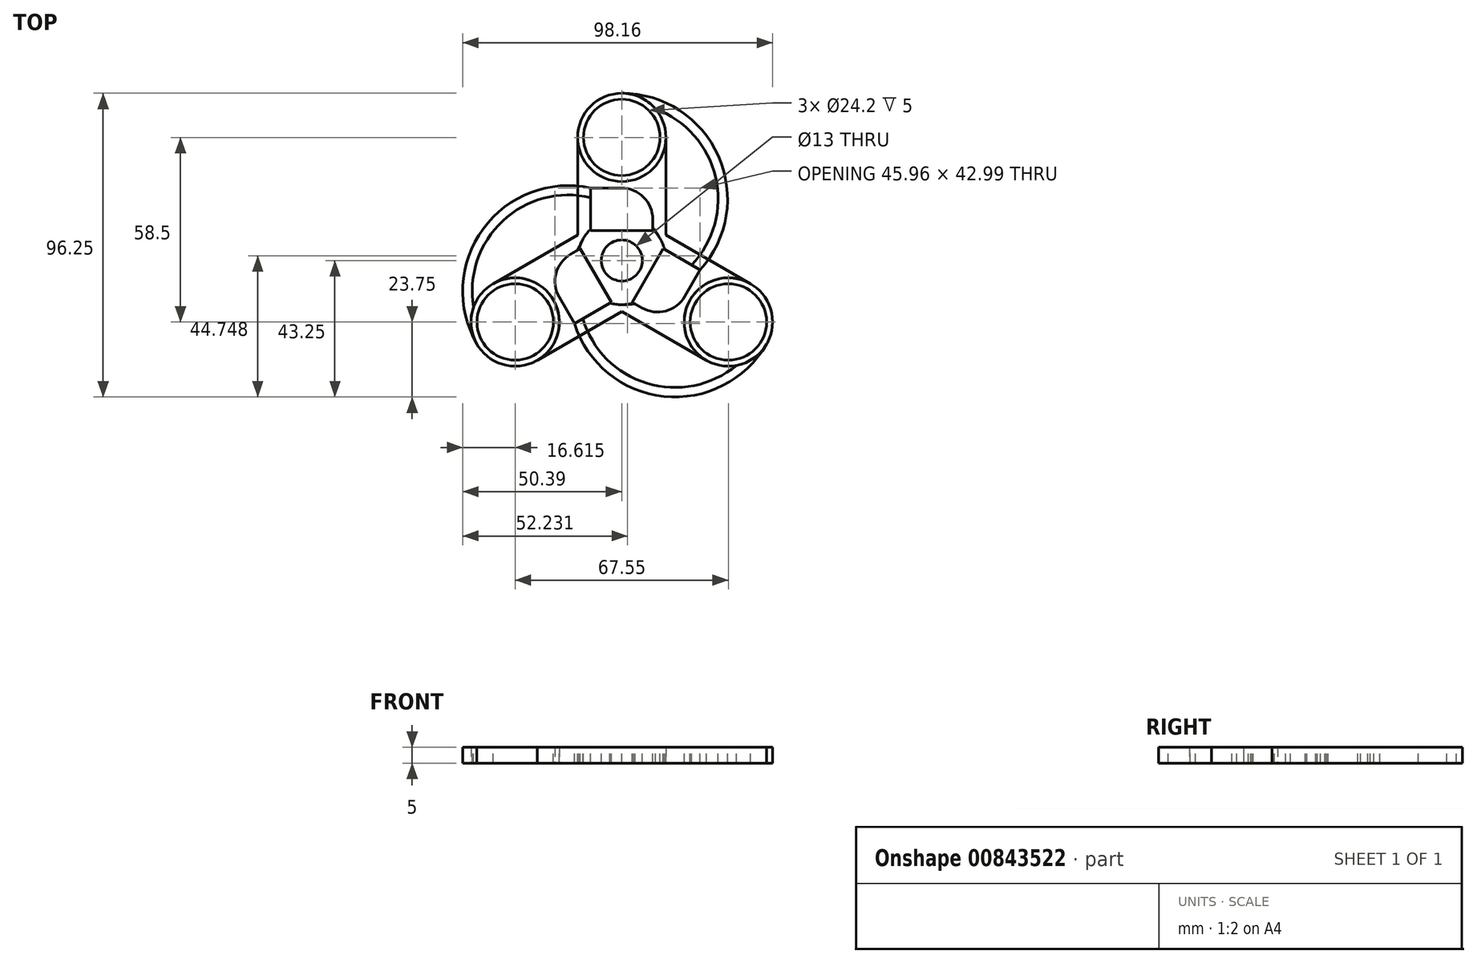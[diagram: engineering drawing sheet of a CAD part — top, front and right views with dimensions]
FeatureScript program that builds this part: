
annotation { "Feature Type Name" : "Feature", "Feature Type Description" : "" }
export const myFeature = defineFeature(function(context is Context, id is Id, definition is map)
    precondition{}
    {
        {
            var Q0;
            Q0=qCreatedBy(makeId("Top.planeOp"),FACE);
            var sketch = newSketch(context, id + "F0", { "sketchPlane" : qUnion([Q0])});
            skCircle(sketch, "E0", {"center": v(0, 0) * mm, "radius": 14 * mm});
            skSolve(sketch);
        }
        {
            var Q0;
            Q0 = qSketchRegion(id + "F0", true);
            extrude(context, id + "F1", {"entities" : qUnion([Q0]), "depth" : 5 * mm, "offsetDistance" : 25 * mm});
        }
        {
            var Q0;
            Q0=makeQuery(id+"F1.opExtrude","CAP_FACE",FACE,{"disambiguationData":[OSD([sQuery(id+"F0.wireOp",EDGE,"E0")])],"isStart":false});
            var sketch = newSketch(context, id + "F2", { "sketchPlane" : qUnion([Q0])});
            skCircle(sketch, "E1", {"center": v(0, 0) * mm, "radius": 6.5 * mm});
            skSolve(sketch);
        }
        {
            var Q0;
            Q0 = qSketchRegion(id + "F2", true);
            var Q1;
            Q1 = qSketchRegion(id + "F4", true);
            extrude(context, id + "F3", {"entities" : qUnion([Q0, Q1]), "operationType" : NewBodyOperationType.REMOVE, "oppositeDirection" : true, "depth" : 5 * mm, "offsetDistance" : 25 * mm});
        }
        {
            var Q0;
            Q0=qCreatedBy(makeId("Top.planeOp"),FACE);
            var sketch = newSketch(context, id + "F4", { "sketchPlane" : qUnion([Q0])});
            skCircle(sketch, "E2", {"center": v(0, 39) * mm, "radius": 14 * mm});
            skCircle(sketch, "E3.1.0", {"center": v(-33.77, -19.5) * mm, "radius": 14 * mm});
            skCircle(sketch, "E3.2.0", {"center": v(33.77, -19.5) * mm, "radius": 14 * mm});
            skPoint(sketch, "E3.center", {"position": v(0, 0) * mm});
            skSolve(sketch);
        }
        {
            var Q0;
            Q0 = qSketchRegion(id + "F4", true);
            extrude(context, id + "F5", {"entities" : qUnion([Q0]), "depth" : 5 * mm, "offsetDistance" : 25 * mm});
        }
        {
            var Q0;
            Q0=makeQuery(id+"F5.opExtrude","CAP_FACE",FACE,{"disambiguationData":[OSD([sQuery(id+"F4.wireOp",EDGE,"E2")])],"isStart":false});
            var sketch = newSketch(context, id + "F6", { "sketchPlane" : qUnion([Q0])});
            skCircle(sketch, "E4", {"center": v(0, 39) * mm, "radius": 12.1 * mm});
            skCircle(sketch, "E5.1.0", {"center": v(-33.77, -19.5) * mm, "radius": 12.1 * mm});
            skCircle(sketch, "E5.2.0", {"center": v(33.77, -19.5) * mm, "radius": 12.1 * mm});
            skPoint(sketch, "E5.center", {"position": v(0, 0) * mm});
            skSolve(sketch);
        }
        {
            var Q0;
            Q0 = qSketchRegion(id + "F6", true);
            extrude(context, id + "F7", {"entities" : qUnion([Q0]), "operationType" : NewBodyOperationType.REMOVE, "oppositeDirection" : true, "depth" : 5 * mm, "offsetDistance" : 25 * mm});
        }
        {
            var Q0;
            Q0=makeQuery(id+"F5.opExtrude","CAP_FACE",FACE,{"disambiguationData":[OSD([sQuery(id+"F4.wireOp",EDGE,"E2")])],"isStart":false});
            var sketch = newSketch(context, id + "F8", { "sketchPlane" : qUnion([Q0])});
            skArc(sketch, "E6", {"start": v(0, -14) * mm, "mid": v(33.5, 19.5) * mm, "end": v(0, 53) * mm});
            skArc(sketch, "E7", {"start": v(10.66, -9.08) * mm, "mid": v(30.5, 19.5) * mm, "end": v(10.66, 48.08) * mm});
            skPoint(sketch, "E7.endSnap0", {"position": v(10.66, 48.08) * mm});
            skArc(sketch, "E8", {"start": v(10.66, 48.08) * mm, "mid": v(5.87, 51.7) * mm, "end": v(0, 53) * mm});
            skArc(sketch, "E9", {"start": v(0, -14) * mm, "mid": v(5.87, -12.7) * mm, "end": v(10.66, -9.08) * mm});
            skArc(sketch, "E10.1.0", {"start": v(12.12, 7) * mm, "mid": v(-33.64, 19.26) * mm, "end": v(-45.9, -26.5) * mm});
            skArc(sketch, "E10.1.1", {"start": v(12.12, 7) * mm, "mid": v(8.07, 11.44) * mm, "end": v(2.53, 13.77) * mm});
            skArc(sketch, "E10.1.2", {"start": v(-46.97, -14.8) * mm, "mid": v(-47.72, -20.77) * mm, "end": v(-45.9, -26.5) * mm});
            skPoint(sketch, "E10.1.3", {"position": v(-46.97, -14.8) * mm});
            skArc(sketch, "E10.1.5", {"start": v(2.53, 13.77) * mm, "mid": v(-32.14, 16.66) * mm, "end": v(-46.97, -14.8) * mm});
            skArc(sketch, "E10.2.0", {"start": v(-12.12, 7) * mm, "mid": v(0.14, -38.76) * mm, "end": v(45.9, -26.5) * mm});
            skArc(sketch, "E10.2.1", {"start": v(-12.12, 7) * mm, "mid": v(-13.94, 1.27) * mm, "end": v(-13.2, -4.7) * mm});
            skArc(sketch, "E10.2.2", {"start": v(36.3, -33.27) * mm, "mid": v(41.85, -30.94) * mm, "end": v(45.9, -26.5) * mm});
            skPoint(sketch, "E10.2.3", {"position": v(36.3, -33.27) * mm});
            skArc(sketch, "E10.2.5", {"start": v(-13.2, -4.7) * mm, "mid": v(1.64, -36.16) * mm, "end": v(36.3, -33.27) * mm});
            skSolve(sketch);
        }
        {
            var Q0;
            Q0 = qSketchRegion(id + "F8", true);
            extrude(context, id + "F9", {"entities" : qUnion([Q0]), "oppositeDirection" : true, "depth" : 5 * mm, "offsetDistance" : 25 * mm});
        }
        {
            var Q0;
            Q0=makeQuery(id+"F9.opExtrude","CAP_FACE",FACE,{"disambiguationData":[OSD([sQuery(id+"F8.wireOp",EDGE,"E6"),sQuery(id+"F8.wireOp",EDGE,"dLtM4N0n-psE5-noLE-qL9G-tePY1SIvNnSB"),sQuery(id+"F8.wireOp",EDGE,"YNhRmu4X-lJfx-RaQj-FMsx-qZMkfT5EsRf2"),sQuery(id+"F8.wireOp",EDGE,"4TdKvFUL-VVMQ-oNHD-A8zk-RRuQfqVaMpFy"),sQuery(id+"F8.wireOp",EDGE,"a4ac8118-5000-4600-9653-84e8d269efdb.1.0"),sQuery(id+"F8.wireOp",EDGE,"a4ac8118-5000-4600-9653-84e8d269efdb.1.1"),sQuery(id+"F8.wireOp",EDGE,"a4ac8118-5000-4600-9653-84e8d269efdb.1.2"),sQuery(id+"F8.wireOp",EDGE,"a4ac8118-5000-4600-9653-84e8d269efdb.1.3"),sQuery(id+"F8.wireOp",EDGE,"a4ac8118-5000-4600-9653-84e8d269efdb.2.0"),sQuery(id+"F8.wireOp",EDGE,"a4ac8118-5000-4600-9653-84e8d269efdb.2.1"),sQuery(id+"F8.wireOp",EDGE,"a4ac8118-5000-4600-9653-84e8d269efdb.2.2"),sQuery(id+"F8.wireOp",EDGE,"a4ac8118-5000-4600-9653-84e8d269efdb.2.3")])],"isStart":true});
            var sketch = newSketch(context, id + "F10", { "sketchPlane" : qUnion([Q0])});
            skLineSegment(sketch, "E11.left", {"start": v(-14, 0) * mm, "end": v(-14, 39) * mm});
            skLineSegment(sketch, "E11.right", {"start": v(14, 0) * mm, "end": v(14, 39) * mm});
            skPoint(sketch, "E12.center", {"position": v(0, 0) * mm});
            skArc(sketch, "E13", {"start": v(-14, 39) * mm, "mid": v(0, 25) * mm, "end": v(14, 39) * mm});
            skArc(sketch, "E14", {"start": v(14, 0) * mm, "mid": v(0, 14) * mm, "end": v(-14, 0) * mm});
            skArc(sketch, "E15.1.0", {"start": v(-7, 12.12) * mm, "mid": v(-12.12, -7) * mm, "end": v(7, -12.12) * mm});
            skLineSegment(sketch, "E15.1.1", {"start": v(-7, 12.12) * mm, "end": v(-40.77, -7.38) * mm});
            skArc(sketch, "E15.1.2", {"start": v(-26.77, -31.62) * mm, "mid": v(-21.65, -12.5) * mm, "end": v(-40.77, -7.38) * mm});
            skLineSegment(sketch, "E15.1.3", {"start": v(7, -12.12) * mm, "end": v(-26.77, -31.62) * mm});
            skArc(sketch, "E15.2.0", {"start": v(-7, -12.12) * mm, "mid": v(12.12, -7) * mm, "end": v(7, 12.12) * mm});
            skLineSegment(sketch, "E15.2.1", {"start": v(-7, -12.12) * mm, "end": v(26.77, -31.62) * mm});
            skArc(sketch, "E15.2.2", {"start": v(40.77, -7.38) * mm, "mid": v(21.65, -12.5) * mm, "end": v(26.77, -31.62) * mm});
            skLineSegment(sketch, "E15.2.3", {"start": v(7, 12.12) * mm, "end": v(40.77, -7.38) * mm});
            skSolve(sketch);
        }
        {
            var Q0;
            Q0 = qSketchRegion(id + "F10", true);
            extrude(context, id + "F11", {"entities" : qUnion([Q0]), "oppositeDirection" : true, "depth" : 5 * mm, "offsetDistance" : 25 * mm});
        }
        {
            var Q0;
            Q0=makeQuery(id+"F11.opExtrude","CAP_FACE",FACE,{"disambiguationData":[OSD([sQuery(id+"F10.wireOp",EDGE,"E11.left"),sQuery(id+"F10.wireOp",EDGE,"E11.right"),sQuery(id+"F10.wireOp",EDGE,"hN4BZvGk-1qVe-ZOfr-WpqT-LToRu9J0DKla"),sQuery(id+"F10.wireOp",EDGE,"Luigv747-6fCb-MAFC-Kryx-cmcWGGftAfeH"),sQuery(id+"F10.wireOp",EDGE,"302ebeea-b909-4b15-a188-612c03519ea0.1.0"),sQuery(id+"F10.wireOp",EDGE,"302ebeea-b909-4b15-a188-612c03519ea0.1.1"),sQuery(id+"F10.wireOp",EDGE,"302ebeea-b909-4b15-a188-612c03519ea0.1.2"),sQuery(id+"F10.wireOp",EDGE,"302ebeea-b909-4b15-a188-612c03519ea0.1.3"),sQuery(id+"F10.wireOp",EDGE,"302ebeea-b909-4b15-a188-612c03519ea0.2.0"),sQuery(id+"F10.wireOp",EDGE,"302ebeea-b909-4b15-a188-612c03519ea0.2.1"),sQuery(id+"F10.wireOp",EDGE,"302ebeea-b909-4b15-a188-612c03519ea0.2.2"),sQuery(id+"F10.wireOp",EDGE,"302ebeea-b909-4b15-a188-612c03519ea0.2.3")])],"isStart":true});
            var sketch = newSketch(context, id + "F12", { "sketchPlane" : qUnion([Q0])});
            skLineSegment(sketch, "E16.bottom", {"start": v(9.82, 9.5) * mm, "end": v(-9.82, 9.5) * mm});
            skLineSegment(sketch, "E16.top", {"start": v(9.82, 23) * mm, "end": v(-9.82, 23) * mm});
            skLineSegment(sketch, "E16.left", {"start": v(9.82, 9.5) * mm, "end": v(9.82, 23) * mm});
            skLineSegment(sketch, "E16.right", {"start": v(-9.82, 9.5) * mm, "end": v(-9.82, 23) * mm});
            skPoint(sketch, "E16.middle", {"position": v(0, 16.25) * mm});
            skLineSegment(sketch, "E17.1.0", {"start": v(-13.13, 3.75) * mm, "end": v(-3.32, -13.25) * mm});
            skLineSegment(sketch, "E17.1.1", {"start": v(-24.82, -3) * mm, "end": v(-15, -20) * mm});
            skLineSegment(sketch, "E17.1.2", {"start": v(-13.13, 3.75) * mm, "end": v(-24.82, -3) * mm});
            skPoint(sketch, "E17.1.3", {"position": v(-14.07, -8.12) * mm});
            skLineSegment(sketch, "E17.1.4", {"start": v(-3.32, -13.25) * mm, "end": v(-15, -20) * mm});
            skLineSegment(sketch, "E17.2.0", {"start": v(3.32, -13.25) * mm, "end": v(13.13, 3.75) * mm});
            skLineSegment(sketch, "E17.2.1", {"start": v(15, -20) * mm, "end": v(24.82, -3) * mm});
            skLineSegment(sketch, "E17.2.2", {"start": v(3.32, -13.25) * mm, "end": v(15, -20) * mm});
            skPoint(sketch, "E17.2.3", {"position": v(14.07, -8.12) * mm});
            skLineSegment(sketch, "E17.2.4", {"start": v(13.13, 3.75) * mm, "end": v(24.82, -3) * mm});
            skPoint(sketch, "E17.center", {"position": v(0, 0) * mm});
            skSolve(sketch);
        }
        {
            var Q0;
            Q0 = qSketchRegion(id + "F12", true);
            extrude(context, id + "F13", {"entities" : qUnion([Q0]), "operationType" : NewBodyOperationType.REMOVE, "oppositeDirection" : true, "depth" : 25 * mm, "offsetDistance" : 25 * mm});
        }
        {
            var Q0;
            Q0=makeQuery(id+"F13.boolean.opBoolean","COPY",EDGE,{"derivedFrom":makeQuery(id+"F13.opExtrude","SWEPT_EDGE",EDGE,{"disambiguationData":[OSD([sQuery(id+"F12.wireOp",EDGE,"E16.top"),sQuery(id+"F12.wireOp",EDGE,"E16.left")])]})});
            var Q1;
            Q1=makeQuery(id+"F13.boolean.opBoolean","COPY",EDGE,{"derivedFrom":makeQuery(id+"F13.opExtrude","SWEPT_EDGE",EDGE,{"disambiguationData":[OSD([sQuery(id+"F12.wireOp",EDGE,"E17.2.1"),sQuery(id+"F12.wireOp",EDGE,"E17.2.2")])]})});
            var Q2;
            Q2=makeQuery(id+"F13.boolean.opBoolean","COPY",EDGE,{"derivedFrom":makeQuery(id+"F13.opExtrude","SWEPT_EDGE",EDGE,{"disambiguationData":[OSD([sQuery(id+"F12.wireOp",EDGE,"E17.1.1"),sQuery(id+"F12.wireOp",EDGE,"E17.1.2")])]})});
            fillet(context, id + "F14", {"entities" : qUnion([Q0, Q1, Q2]), "radius" : 10 * mm, "tangentPropagation" : true, "allowEdgeOverflow" : false});
        }
    });
